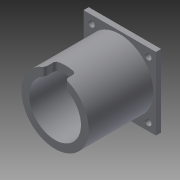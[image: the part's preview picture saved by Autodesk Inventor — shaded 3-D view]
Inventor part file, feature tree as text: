
AUTODESK INVENTOR PART (.ipt)
format: ipt  version: 2015 (Build 190159000, 159)  size: 151,552 bytes
history: native  units: in
note: dims shown in document units (in); Inventor stores cm internally (conversion verified against a paired STEP export)
features: sketch x5, extrude x4, hole x1, plane x1, fillet x1
ambient origin geometry x8: Origin, YZ Plane, XZ Plane, XY Plane, X Axis, Y Axis, Z Axis, Center Point
bodies: Solid1 (feature_tree)
feature tree (12):
  extrude  "Extrusion1"  Depth=1.4in
  extrude  "Extrusion2"  Depth=0.7in
  hole  "Hole1"  [1 undecoded]
  plane  "Work Plane1"
  extrude  "Extrusion3"  Depth=1.25in TaperAngle=0.0deg
  extrude  "Extrusion4"  Depth=0.05in
  fillet  "Fillet1"  Radius=0.15in
  sketch  "Sketch1"  dims[d0=1.4in d1=1.4in]
  sketch  "Sketch2"  dims[d2=0.7in d3=0.7in]
  sketch  "Sketch3"  dims[d4=0.1in d5=0.0in d6=1.0in]
  sketch  "Sketch4"  dims[d7=0.15in d8=1.25in d9=0.0in]
  sketch  "Sketch5"  dims[d10=0.15in d11=0.15in d12=0.15in d13=0.15in d14=0.15in d15=0.15in d16=0.15in d17=0.15in d18=0.125in d19=0.75in d20=0.375in d21=0.25in d22=0.5635in d23=0.125in d24=0.8108in d25=0.65in d26=0.2in d27=0.4in d28=0.2in d29=0.4in d30=0.0in d31=0.35in d32=0.4in d33=0.0in d34=0.05in]
note: 1 required parameter value undecoded (feature->parameter linkage not recoverable at this tier; creation-order binding heuristic only, values carry confidence <= 0.55)
